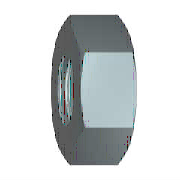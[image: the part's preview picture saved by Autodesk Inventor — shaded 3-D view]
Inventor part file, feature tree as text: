
AUTODESK INVENTOR PART (.ipt)
format: ipt  version: 2019 (Build 230136000, 136)  size: 184,832 bytes
history: native  units: mm (DEFAULTED — no unit token found)
features: sketch x3, chamfer x1, hole x1, other x1, plane x1
ambient origin geometry x7: Origin, YZ Plane, XZ Plane, X Axis, Y Axis, Z Axis, Center Point
bodies: Solid1 (feature_tree), Body (feature_tree)
feature tree (7):
  chamfer  "Chamfer1"  Angle=30.0deg  [1 undecoded]
  hole  "Thread"  [1 undecoded]
  other  "Work Axis1"
  plane  "Work Plane1"
  sketch  "Sketch1"  dims[d0=6.350853mm]
  sketch  "Sketch2"  dims[d1=2.4mm]
  sketch  "Sketch3"  dims[d2=0.0mm d3=30.0deg d4=30.0deg d5=5.5mm d6=5.5mm d7=90.0deg d25=2.459mm d26=6.0mm d27=4.0mm d28=2.0mm d29=14.3117mm d30=8.0mm d31=20.594885mm d8=0.270633mm d9=30.0deg d10=0.270633mm d11=30.0deg d13=0.0mm d14=0.0mm d39=0.0mm d40=0.270633mm d41=0.270633mm d42=0.0mm]
note: 2 required parameter values undecoded (feature->parameter linkage not recoverable at this tier; creation-order binding heuristic only, values carry confidence <= 0.55)
